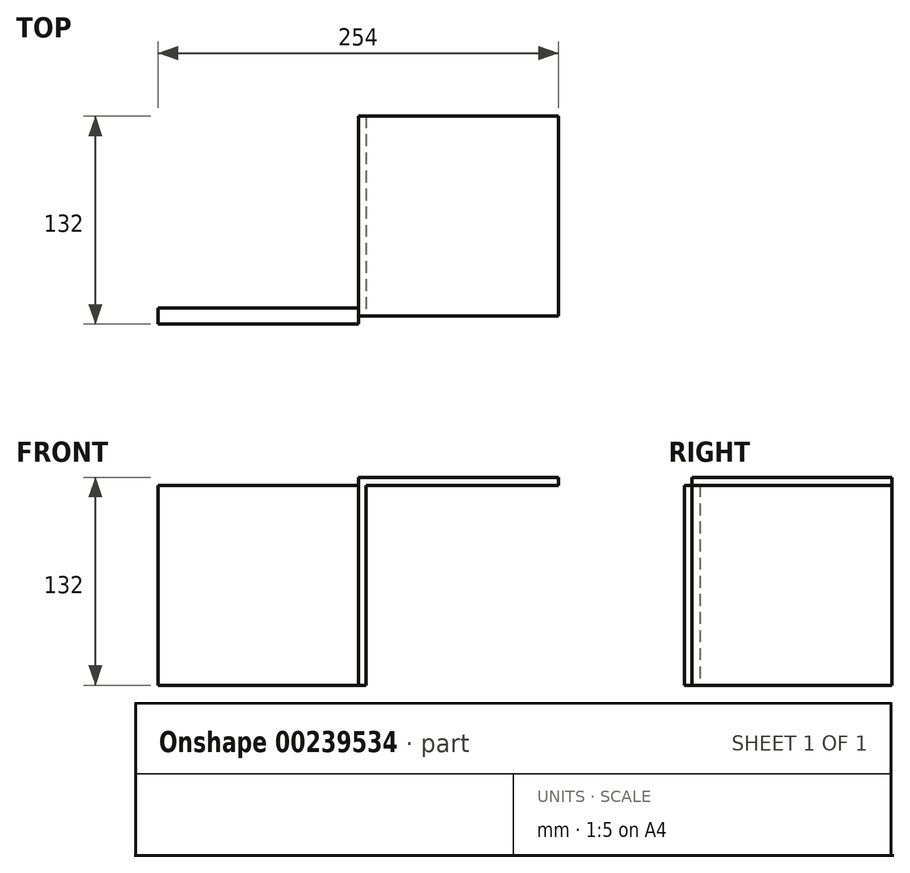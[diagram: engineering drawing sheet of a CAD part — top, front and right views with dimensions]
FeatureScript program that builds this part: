
annotation { "Feature Type Name" : "Feature", "Feature Type Description" : "" }
export const myFeature = defineFeature(function(context is Context, id is Id, definition is map)
    precondition{}
    {
        {
            assignVariable(context, id + "F0", {"name" : "L", "anyValue" : 5});
        }
        {
            var Q0;
            Q0=qCreatedBy(makeId("Front.planeOp"),FACE);
            var sketch = newSketch(context, id + "F1", { "sketchPlane" : qUnion([Q0])});
            skLineSegment(sketch, "E0.bottom", {"start": v(-63.5, 63.5) * mm, "end": v(63.5, 63.5) * mm});
            skLineSegment(sketch, "E0.top", {"start": v(-63.5, -63.5) * mm, "end": v(63.5, -63.5) * mm});
            skLineSegment(sketch, "E0.left", {"start": v(-63.5, 63.5) * mm, "end": v(-63.5, -63.5) * mm});
            skLineSegment(sketch, "E0.right", {"start": v(63.5, 63.5) * mm, "end": v(63.5, -63.5) * mm});
            skPoint(sketch, "E0.middle", {"position": v(0, 0) * mm});
            skSolve(sketch);
        }
        {
            var Q0;
            Q0 = qSketchRegion(id + "F1", true);
            extrude(context, id + "F2", {"entities" : qUnion([Q0]), "endBound" : BoundingType.SYMMETRIC, "oppositeDirection" : true, "depth" : (getVariable(context, 'L') * 2) * mm});
        }
        {
            var Q0;
            Q0=makeQuery(id+"F2.opExtrude","SWEPT_FACE",FACE,{"disambiguationData":[OSD([sQuery(id+"F1.wireOp",EDGE,"E0.right")])]});
            var sketch = newSketch(context, id + "F3", { "sketchPlane" : qUnion([Q0])});
            skLineSegment(sketch, "E1.bottom", {"start": v(127, 63.5) * mm, "end": v(0, 63.5) * mm});
            skLineSegment(sketch, "E1.top", {"start": v(127, -63.5) * mm, "end": v(0, -63.5) * mm});
            skLineSegment(sketch, "E1.left", {"start": v(127, 63.5) * mm, "end": v(127, -63.5) * mm});
            skLineSegment(sketch, "E1.right", {"start": v(0, 63.5) * mm, "end": v(0, -63.5) * mm});
            skSolve(sketch);
        }
        {
            var Q0;
            Q0 = qSketchRegion(id + "F3", true);
            extrude(context, id + "F4", {"entities" : qUnion([Q0]), "operationType" : NewBodyOperationType.ADD, "depth" : (getVariable(context, 'L')) * mm});
        }
        {
            var Q0;
            Q0=makeQuery(id+"F4.boolean.opBoolean","MERGE",FACE,{"derivedFrom":[makeQuery(id+"F2.opExtrude","SWEPT_FACE",FACE,{"disambiguationData":[OSD([sQuery(id+"F1.wireOp",EDGE,"E0.bottom")])]}),makeQuery(id+"F4.opExtrude","SWEPT_FACE",FACE,{"disambiguationData":[OSD([sQuery(id+"F3.wireOp",EDGE,"E1.bottom")])]})]});
            var sketch = newSketch(context, id + "F5", { "sketchPlane" : qUnion([Q0])});
            skLineSegment(sketch, "E2.bottom", {"start": v(63.5, 0) * mm, "end": v(190.5, 0) * mm});
            skLineSegment(sketch, "E2.top", {"start": v(63.5, 127) * mm, "end": v(190.5, 127) * mm});
            skLineSegment(sketch, "E2.left", {"start": v(63.5, 0) * mm, "end": v(63.5, 127) * mm});
            skLineSegment(sketch, "E2.right", {"start": v(190.5, 0) * mm, "end": v(190.5, 127) * mm});
            skSolve(sketch);
        }
        {
            var Q0;
            Q0 = qSketchRegion(id + "F5", true);
            extrude(context, id + "F6", {"entities" : qUnion([Q0]), "operationType" : NewBodyOperationType.ADD, "depth" : (getVariable(context, 'L')) * mm});
        }
    });
